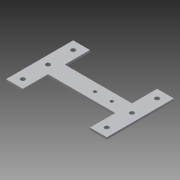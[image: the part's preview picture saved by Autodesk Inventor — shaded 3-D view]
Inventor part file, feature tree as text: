
AUTODESK INVENTOR PART (.ipt)
format: ipt  version: 2013 (Build 170138000, 138)  size: 155,136 bytes
history: native  units: in
note: dims shown in document units (in); Inventor stores cm internally (conversion verified against a paired STEP export)
features: other x5, sketch x4, sheet_metal_op x3
ambient origin geometry x8: Origin, YZ Plane, XZ Plane, XY Plane, X Axis, Y Axis, Z Axis, Center Point
bodies: Solid1 (feature_tree)
feature tree (12):
  sheet_metal_op  "Face1"
  sheet_metal_op  "Face2"
  other  "Plate1"
  sketch  "Sketch5"  dims[d0=1.0in]
  sketch  "Sketch10"  dims[d1=6.0in]
  sketch  "Sketch12"  dims[d2=0.125in]
  sketch  "Sketch13"  dims[d33=0.2in d34=0.2in d35=1.0in d37=0.125in d38=0.0in d55=0.5in d56=0.5in d57=2.2in d58=1.5in d59=1.0in d60=0.266in d61=0.5in d62=0.5in d63=0.266in d64=0.5in d65=0.5in d66=0.125in d67=0.0in d71=0.125in d72=0.0in d73=1.0in d74=1.5in d75=1.0in d76=1.5in d77=1.0in d78=0.266in d79=0.266in d80=0.266in d81=0.5in d82=0.5in d83=0.5in d84=0.5in d85=0.5in d86=0.5in d87=1.5in d88=0.125in d89=0.125in d90=0.0625in d91=0.25in d92=0.125in]
  other  "Plate5"
  sheet_metal_op  "Bend4"
  other  "Cut1"
  other  "Cut6"
  other  "Cut7"
